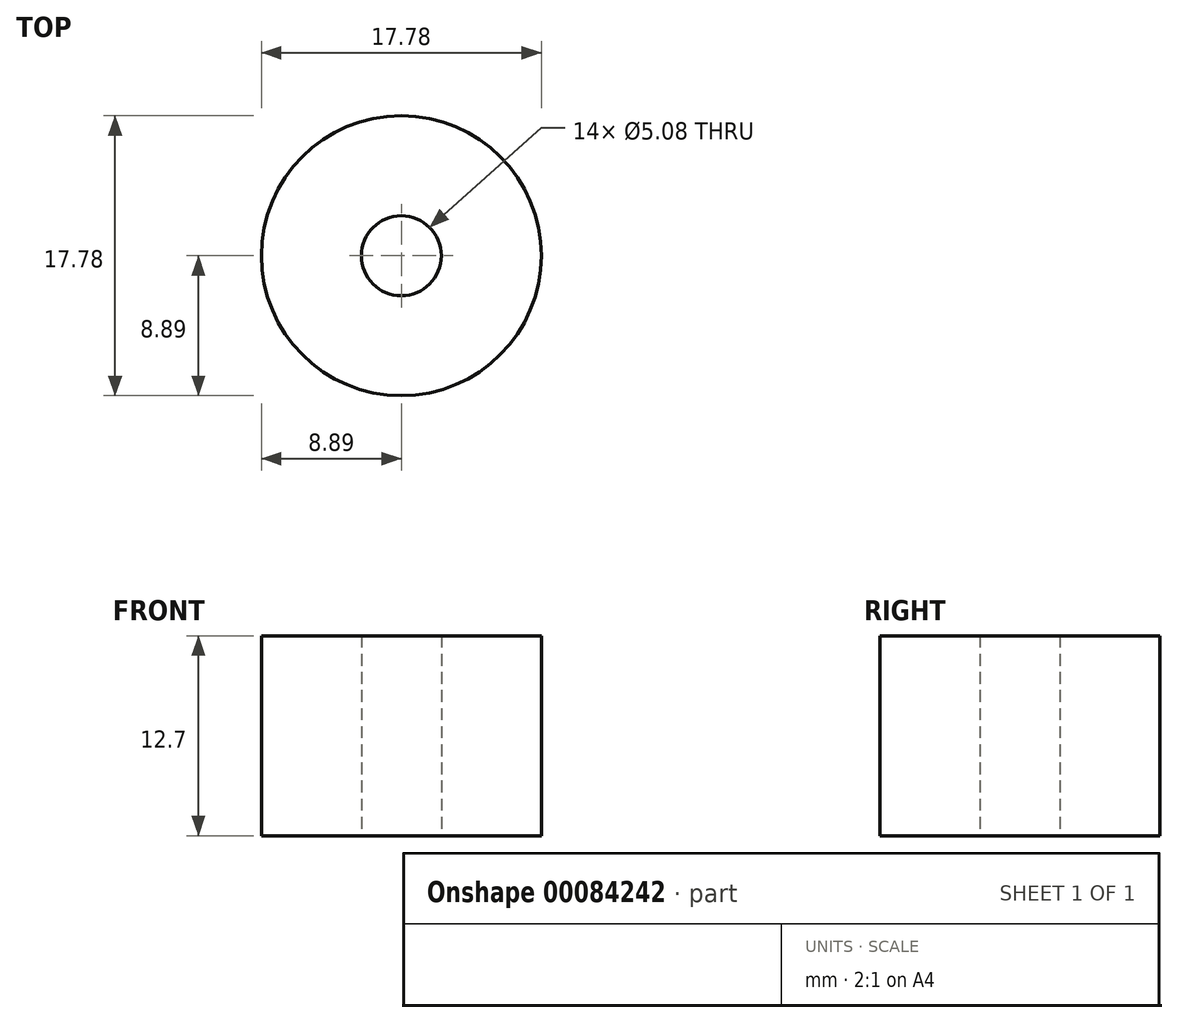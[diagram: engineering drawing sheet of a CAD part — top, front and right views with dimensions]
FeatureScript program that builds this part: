
annotation { "Feature Type Name" : "Feature", "Feature Type Description" : "" }
export const myFeature = defineFeature(function(context is Context, id is Id, definition is map)
    precondition{}
    {
        {
            var Q0;
            Q0=qCreatedBy(makeId("Top.planeOp"),FACE);
            var sketch = newSketch(context, id + "F0", { "sketchPlane" : qUnion([Q0])});
            skCircle(sketch, "E0", {"center": v(0, 0) * mm, "radius": 8.89 * mm});
            skCircle(sketch, "E1", {"center": v(0, 0) * mm, "radius": 2.54 * mm});
            skSolve(sketch);
        }
        {
            var Q0;
            Q0 = qSketchRegion(id + "F0", true);
            extrude(context, id + "F1", {"entities" : qUnion([Q0]), "endBound" : BoundingType.SYMMETRIC, "depth" : 12.7 * mm});
        }
    });
